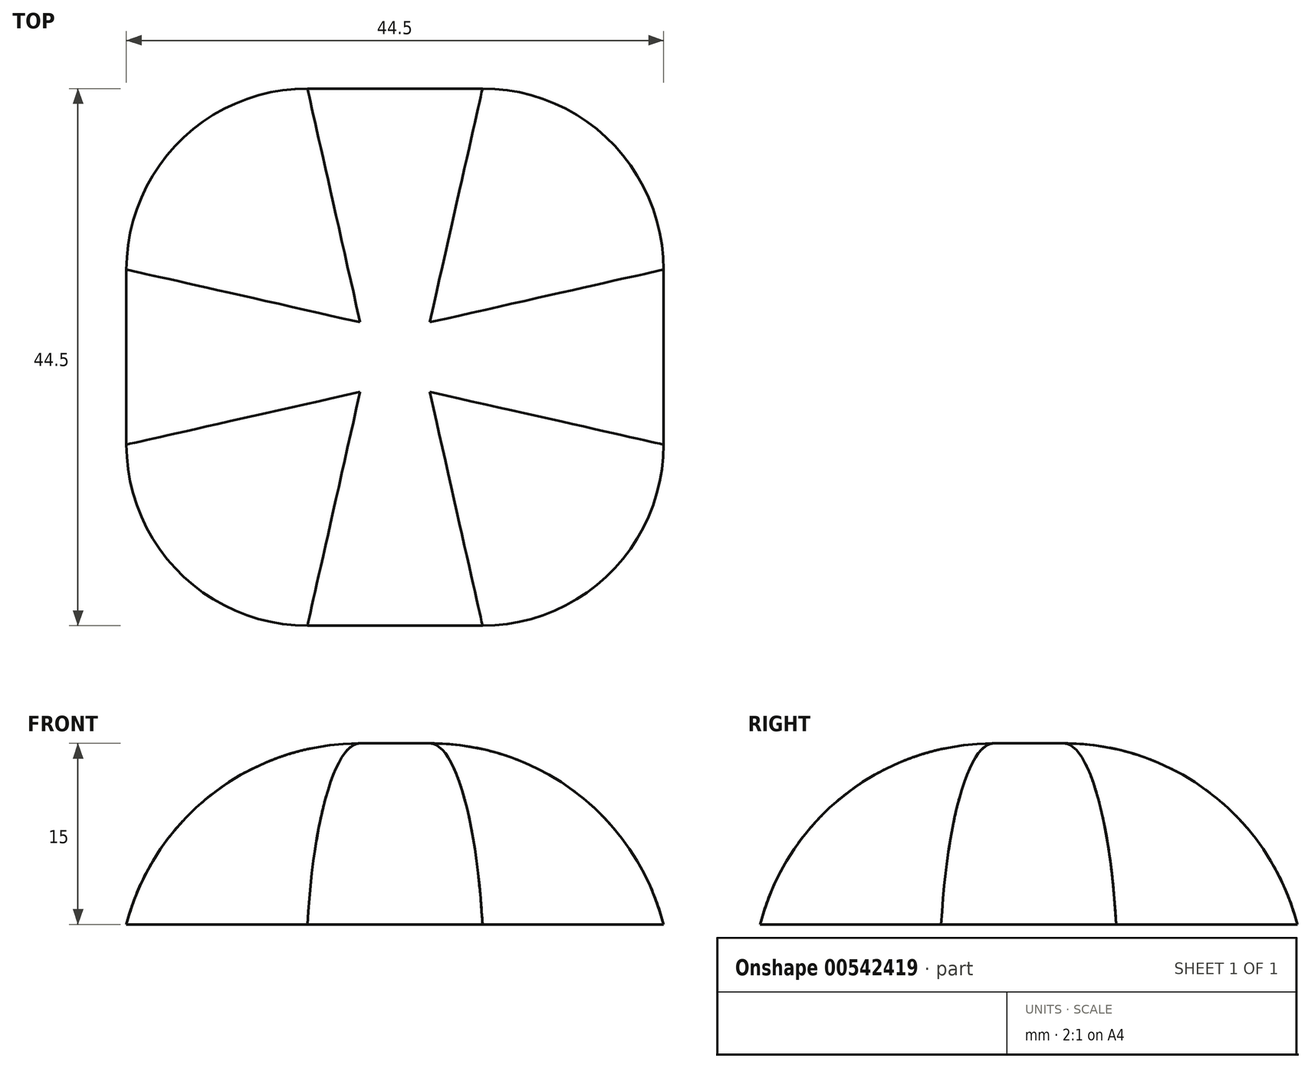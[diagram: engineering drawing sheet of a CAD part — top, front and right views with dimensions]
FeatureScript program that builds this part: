
annotation { "Feature Type Name" : "Feature", "Feature Type Description" : "" }
export const myFeature = defineFeature(function(context is Context, id is Id, definition is map)
    precondition{}
    {
        {
            var Q0;
            Q0=qCreatedBy(makeId("Top.planeOp"),FACE);
            var sketch = newSketch(context, id + "F0", { "sketchPlane" : qUnion([Q0])});
            skLineSegment(sketch, "E0.bottom", {"start": v(22.25, 22.25) * mm, "end": v(-22.25, 22.25) * mm});
            skLineSegment(sketch, "E0.top", {"start": v(22.25, -22.25) * mm, "end": v(-22.25, -22.25) * mm});
            skLineSegment(sketch, "E0.left", {"start": v(22.25, 22.25) * mm, "end": v(22.25, -22.25) * mm});
            skLineSegment(sketch, "E0.right", {"start": v(-22.25, 22.25) * mm, "end": v(-22.25, -22.25) * mm});
            skPoint(sketch, "E0.middle", {"position": v(0, 0) * mm});
            skSolve(sketch);
        }
        {
            var Q0;
            Q0=makeQuery(id+"F0.imprint","IMPRINT",FACE,{"disambiguationData":[TD([[makeQuery(id+"F0.imprint","IMPRINT",EDGE,{"derivedFrom":sQuery(id+"F0.wireOp",EDGE,"E0.bottom")}),1.0]])]});
            extrude(context, id + "F1", {"entities" : qUnion([Q0]), "depth" : 15 * mm, "offsetDistance" : 25 * mm});
        }
        {
            var Q0;
            Q0=makeQuery(id+"F1.opExtrude","SWEPT_EDGE",EDGE,{"disambiguationData":[OSD([sQuery(id+"F0.wireOp",EDGE,"E0.top"),sQuery(id+"F0.wireOp",EDGE,"E0.right")])]});
            fillet(context, id + "F2", {"entities" : qUnion([Q0]), "radius" : 15 * mm, "tangentPropagation" : true, "allowEdgeOverflow" : false});
        }
        {
            var Q0;
            Q0=makeQuery(id+"F1.opExtrude","SWEPT_EDGE",EDGE,{"disambiguationData":[OSD([sQuery(id+"F0.wireOp",EDGE,"E0.top"),sQuery(id+"F0.wireOp",EDGE,"E0.left")])]});
            fillet(context, id + "F3", {"entities" : qUnion([Q0]), "radius" : 15 * mm, "tangentPropagation" : true, "allowEdgeOverflow" : false});
        }
        {
            var Q0;
            Q0=makeQuery(id+"F1.opExtrude","SWEPT_EDGE",EDGE,{"disambiguationData":[OSD([sQuery(id+"F0.wireOp",EDGE,"E0.bottom"),sQuery(id+"F0.wireOp",EDGE,"E0.right")])]});
            fillet(context, id + "F4", {"entities" : qUnion([Q0]), "radius" : 15 * mm, "tangentPropagation" : true, "allowEdgeOverflow" : false});
        }
        {
            var Q0;
            Q0=makeQuery(id+"F1.opExtrude","SWEPT_EDGE",EDGE,{"disambiguationData":[OSD([sQuery(id+"F0.wireOp",EDGE,"E0.bottom"),sQuery(id+"F0.wireOp",EDGE,"E0.left")])]});
            fillet(context, id + "F5", {"entities" : qUnion([Q0]), "radius" : 15 * mm, "tangentPropagation" : true, "allowEdgeOverflow" : false});
        }
        {
            var Q0;
            Q0=makeQuery(id+"F1.opExtrude","CAP_FACE",FACE,{"disambiguationData":[OSD([sQuery(id+"F0.wireOp",EDGE,"E0.bottom"),sQuery(id+"F0.wireOp",EDGE,"E0.top"),sQuery(id+"F0.wireOp",EDGE,"E0.left"),sQuery(id+"F0.wireOp",EDGE,"E0.right")])],"isStart":false});
            fillet(context, id + "F6", {"entities" : qUnion([Q0]), "radius" : 20 * mm, "tangentPropagation" : true, "allowEdgeOverflow" : false});
        }
    });
